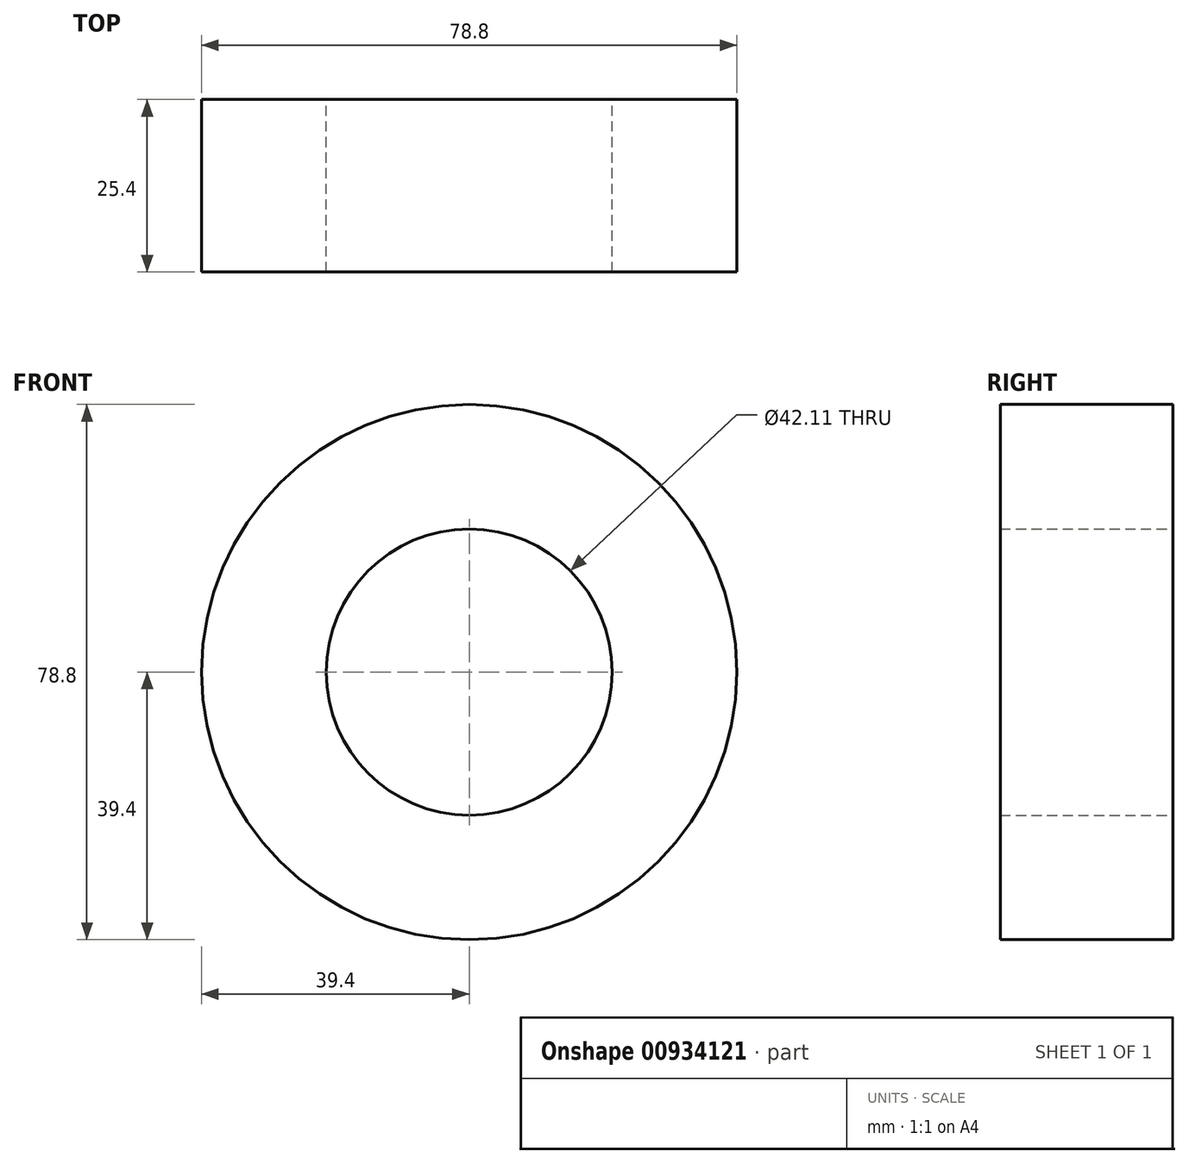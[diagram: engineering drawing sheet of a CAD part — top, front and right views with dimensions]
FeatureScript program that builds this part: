
annotation { "Feature Type Name" : "Feature", "Feature Type Description" : "" }
export const myFeature = defineFeature(function(context is Context, id is Id, definition is map)
    precondition{}
    {
        {
            var Q0;
            Q0=qCreatedBy(makeId("Front.planeOp"),FACE);
            var sketch = newSketch(context, id + "F0", { "sketchPlane" : qUnion([Q0])});
            skCircle(sketch, "E0", {"center": v(0, 0) * mm, "radius": 39.4 * mm});
            skCircle(sketch, "E1", {"center": v(0, 0) * mm, "radius": 21.06 * mm});
            skSolve(sketch);
        }
        {
            var Q0;
            Q0 = qSketchRegion(id + "F0", true);
            extrude(context, id + "F1", {"entities" : qUnion([Q0]), "depth" : 25.4 * mm, "offsetDistance" : 25.4 * mm});
        }
    });
